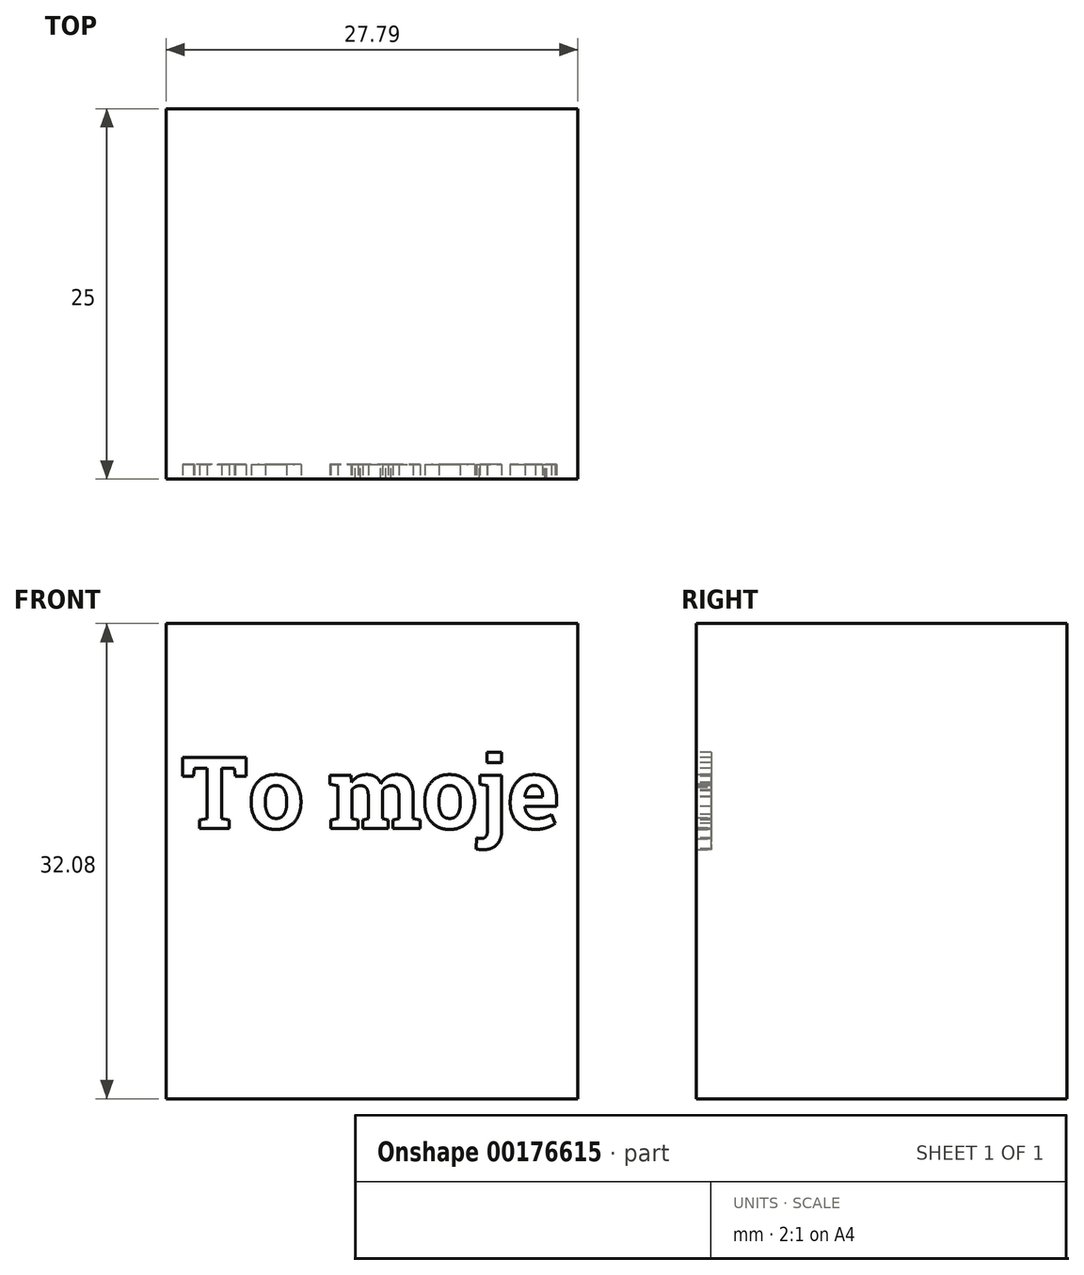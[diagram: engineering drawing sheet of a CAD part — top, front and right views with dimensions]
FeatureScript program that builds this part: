
annotation { "Feature Type Name" : "Feature", "Feature Type Description" : "" }
export const myFeature = defineFeature(function(context is Context, id is Id, definition is map)
    precondition{}
    {
        {
            var Q0;
            Q0=qCreatedBy(makeId("Front.planeOp"),FACE);
            var sketch = newSketch(context, id + "F0", { "sketchPlane" : qUnion([Q0])});
            skLineSegment(sketch, "E0.bottom", {"start": v(-27.8, 32.08) * mm, "end": v(0, 32.08) * mm});
            skLineSegment(sketch, "E0.top", {"start": v(-27.8, 0) * mm, "end": v(0, 0) * mm});
            skLineSegment(sketch, "E0.left", {"start": v(-27.8, 32.08) * mm, "end": v(-27.8, 0) * mm});
            skLineSegment(sketch, "E0.right", {"start": v(0, 32.08) * mm, "end": v(0, 0) * mm});
            skSolve(sketch);
        }
        {
            var Q0;
            Q0=makeQuery(id+"F0.imprint","IMPRINT",FACE,{"disambiguationData":[TD([[makeQuery(id+"F0.imprint","IMPRINT",EDGE,{"derivedFrom":sQuery(id+"F0.wireOp",EDGE,"E0.bottom")}),-1.0]])]});
            extrude(context, id + "F1", {"entities" : qUnion([Q0]), "depth" : 25 * mm});
        }
        {
            var Q0;
            Q0=makeQuery(id+"F1.opExtrude","CAP_FACE",FACE,{"disambiguationData":[OSD([sQuery(id+"F0.wireOp",EDGE,"E0.bottom"),sQuery(id+"F0.wireOp",EDGE,"E0.top"),sQuery(id+"F0.wireOp",EDGE,"E0.left"),sQuery(id+"F0.wireOp",EDGE,"E0.right")])],"isStart":false});
            var sketch = newSketch(context, id + "F2", { "sketchPlane" : qUnion([Q0])});
            skText(sketch, "E1", { "text": "To moje", "fontName": "RobotoSlab-Bold.ttf"});
            const initialGuessF2  = {"E1": [-0.0268, 0.01825, 1, 0, 0.00486]};
            skSetInitialGuess(sketch, initialGuessF2);
            skSolve(sketch);
        }
        {
            var Q0;
            Q0 = qSketchRegion(id + "F2", true);
            extrude(context, id + "F3", {"entities" : qUnion([Q0]), "operationType" : NewBodyOperationType.REMOVE, "oppositeDirection" : true, "depth" : 1 * mm});
        }
    });
